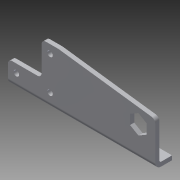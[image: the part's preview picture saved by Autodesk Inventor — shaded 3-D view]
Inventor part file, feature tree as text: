
AUTODESK INVENTOR PART (.ipt)
format: ipt  version: 2014 (Build 180170000, 170)  size: 134,656 bytes
history: native  units: in
note: dims shown in document units (in); Inventor stores cm internally (conversion verified against a paired STEP export)
features: sheet_metal_op x4, sketch x2, other x2, fillet x1
ambient origin geometry x8: Origin, YZ Plane, XZ Plane, XY Plane, X Axis, Y Axis, Z Axis, Center Point
bodies: Solid1 (feature_tree)
feature tree (9):
  sheet_metal_op  "Face1"
  sheet_metal_op  "Flange1"
  fillet  "Fillet2"  Radius=0.5in
  sketch  "Sketch1"  dims[d1=1.0in]
  other  "Plate1"
  sketch  "Sketch2"  dims[d2=1.0in d3=0.5in d4=4.375in d5=0.5in d6=0.75in d7=0.5in d8=90.0deg d9=1.125in d10=0.163in d11=0.25in d12=0.25in d13=0.7874in d15=1.0in d16=0.3937in d18=1.0in d20=0.7874in d22=1.0in d23=0.3937in d25=1.0in d27=0.125in d29=0.125in d30=0.0625in d31=0.25in d32=0.125in d33=0.5in d34=90.0deg d35=0.05in d36=0.5in d37=0.125in d38=0.125in d39=0.125in]
  other  "Plate2"
  sheet_metal_op  "Bend1"
  sheet_metal_op  "Corner1"
